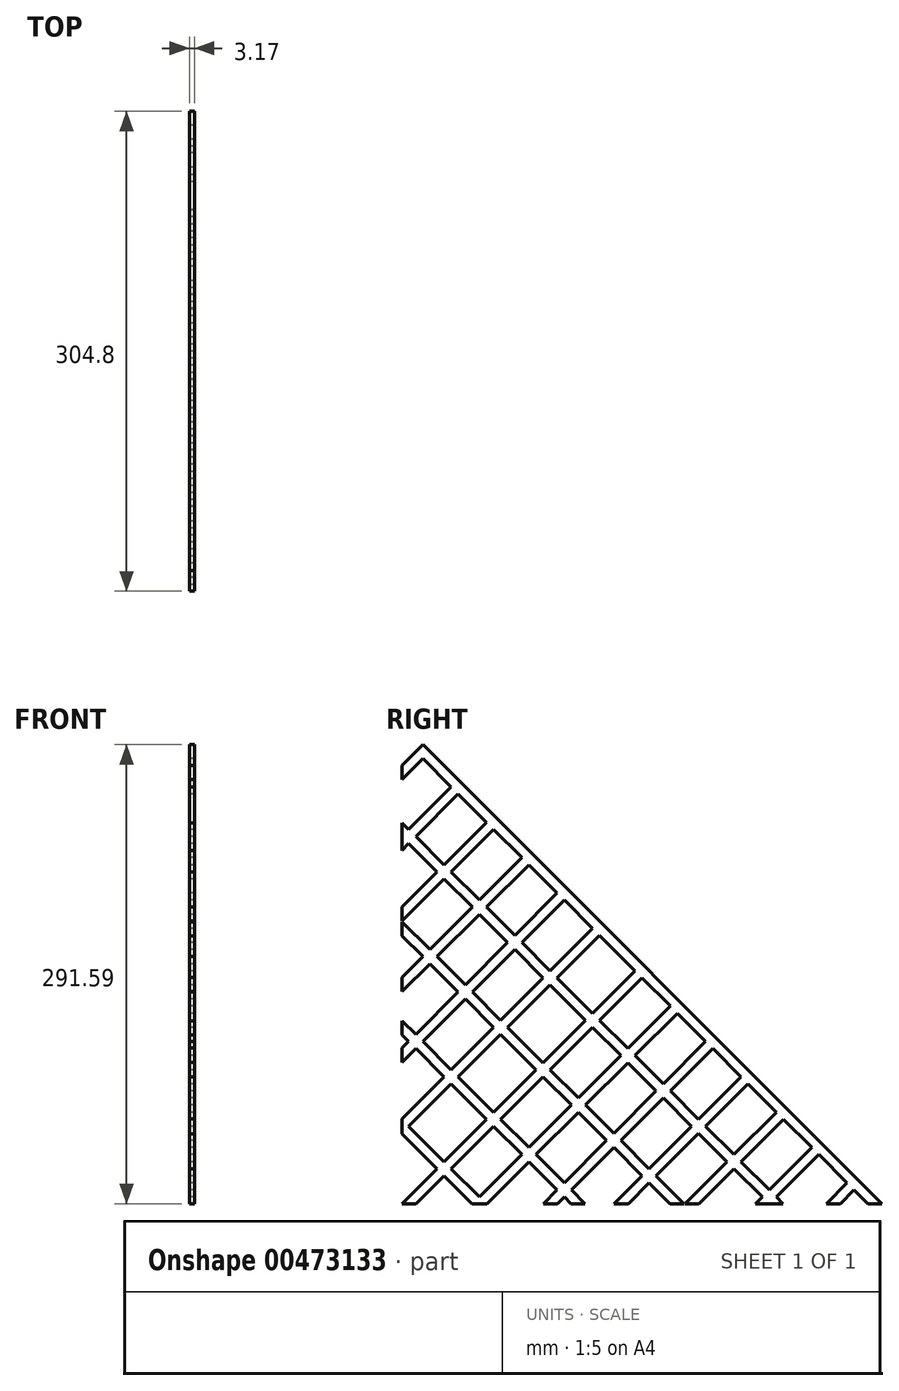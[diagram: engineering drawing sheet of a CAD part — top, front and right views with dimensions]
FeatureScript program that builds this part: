
annotation { "Feature Type Name" : "Feature", "Feature Type Description" : "" }
export const myFeature = defineFeature(function(context is Context, id is Id, definition is map)
    precondition{}
    {
        {
            var Q0;
            Q0=qCreatedBy(makeId("Right.planeOp"),FACE);
            var sketch = newSketch(context, id + "F0", { "sketchPlane" : qUnion([Q0])});
            skLineSegment(sketch, "E0.bottom", {"start": v(0, 0) * mm, "end": v(304.8, 0) * mm, "construction": true});
            skLineSegment(sketch, "E0.top", {"start": v(0, 304.8) * mm, "end": v(304.8, 304.8) * mm, "construction": true});
            skLineSegment(sketch, "E0.left", {"start": v(0, 0) * mm, "end": v(0, 304.8) * mm, "construction": true});
            skLineSegment(sketch, "E0.right", {"start": v(304.8, 0) * mm, "end": v(304.8, 304.8) * mm, "construction": true});
            skLineSegment(sketch, "E1", {"start": v(0, 0) * mm, "end": v(304.8, 304.8) * mm});
            skLineSegment(sketch, "E2.0", {"start": v(4.5, -4.5) * mm, "end": v(309.3, 300.3) * mm});
            skLineSegment(sketch, "E3.0", {"start": v(22.45, -22.45) * mm, "end": v(327.25, 282.35) * mm});
            skLineSegment(sketch, "E4.0", {"start": v(26.94, -26.94) * mm, "end": v(331.74, 277.86) * mm});
            skLineSegment(sketch, "E5.0", {"start": v(44.9, -44.9) * mm, "end": v(349.7, 259.9) * mm});
            skLineSegment(sketch, "E6.0", {"start": v(49.4, -49.4) * mm, "end": v(354.2, 255.4) * mm});
            skLineSegment(sketch, "E7.0", {"start": v(67.35, -67.35) * mm, "end": v(372.15, 237.45) * mm});
            skLineSegment(sketch, "E8.0", {"start": v(71.84, -71.84) * mm, "end": v(376.64, 232.96) * mm});
            skLineSegment(sketch, "E9.0", {"start": v(89.8, -89.8) * mm, "end": v(394.6, 215) * mm});
            skLineSegment(sketch, "E10.0", {"start": v(94.3, -94.3) * mm, "end": v(399.1, 210.5) * mm});
            skLineSegment(sketch, "E11.0", {"start": v(112.25, -112.25) * mm, "end": v(417.05, 192.55) * mm});
            skLineSegment(sketch, "E12.0", {"start": v(116.74, -116.74) * mm, "end": v(421.54, 188.06) * mm});
            skLineSegment(sketch, "E13.0", {"start": v(134.7, -134.7) * mm, "end": v(439.5, 170.1) * mm});
            skLineSegment(sketch, "E14.0", {"start": v(139.2, -139.2) * mm, "end": v(444, 165.6) * mm});
            skLineSegment(sketch, "E15.MirrorCS", {"start": v(-26.94, 26.94) * mm, "end": v(277.86, 331.74) * mm});
            skLineSegment(sketch, "E16.MirrorCS", {"start": v(-22.45, 22.45) * mm, "end": v(282.35, 327.25) * mm});
            skLineSegment(sketch, "E17.MirrorCS", {"start": v(-116.74, 116.74) * mm, "end": v(-27.2, 206.28) * mm});
            skLineSegment(sketch, "E18.MirrorCS", {"start": v(-112.25, 112.25) * mm, "end": v(-22.71, 201.8) * mm});
            skLineSegment(sketch, "E19.MirrorCS", {"start": v(-134.7, 134.7) * mm, "end": v(-13.73, 255.67) * mm});
            skLineSegment(sketch, "E20.MirrorCS", {"start": v(-139.2, 139.2) * mm, "end": v(-18.22, 260.16) * mm});
            skLineSegment(sketch, "E21.MirrorCS", {"start": v(-94.3, 94.3) * mm, "end": v(-4.75, 183.83) * mm});
            skLineSegment(sketch, "E22.MirrorCS", {"start": v(-49.4, 49.4) * mm, "end": v(255.4, 354.2) * mm});
            skLineSegment(sketch, "E23.MirrorCS", {"start": v(-71.84, 71.84) * mm, "end": v(232.96, 376.64) * mm});
            skLineSegment(sketch, "E24.MirrorCS", {"start": v(-67.35, 67.35) * mm, "end": v(237.45, 372.15) * mm});
            skLineSegment(sketch, "E25.MirrorCS", {"start": v(-44.9, 44.9) * mm, "end": v(259.9, 349.7) * mm});
            skLineSegment(sketch, "E26.MirrorCS", {"start": v(-89.8, 89.8) * mm, "end": v(-4.75, 174.85) * mm});
            skLineSegment(sketch, "E27", {"start": v(0, 304.8) * mm, "end": v(304.8, 0) * mm});
            skLineSegment(sketch, "E28.0", {"start": v(-4.5, 300.3) * mm, "end": v(300.3, -4.5) * mm});
            skLineSegment(sketch, "E29.0", {"start": v(-31.43, 273.37) * mm, "end": v(-13.73, 255.67) * mm});
            skLineSegment(sketch, "E30.0", {"start": v(-35.92, 268.88) * mm, "end": v(-18.22, 251.18) * mm});
            skLineSegment(sketch, "E31.0", {"start": v(-62.86, 241.94) * mm, "end": v(-4.75, 183.83) * mm});
            skLineSegment(sketch, "E32.0", {"start": v(-67.35, 237.45) * mm, "end": v(237.45, -67.35) * mm});
            skLineSegment(sketch, "E33.0", {"start": v(-94.3, 210.5) * mm, "end": v(210.5, -94.3) * mm});
            skLineSegment(sketch, "E34.0", {"start": v(-98.78, 206.02) * mm, "end": v(206.02, -98.78) * mm});
            skLineSegment(sketch, "E35.0", {"start": v(-125.72, 179.08) * mm, "end": v(179.08, -125.72) * mm});
            skLineSegment(sketch, "E36.0", {"start": v(-130.21, 174.59) * mm, "end": v(174.59, -130.21) * mm});
            skLineSegment(sketch, "E37.MirrorCS", {"start": v(31.43, 336.23) * mm, "end": v(336.23, 31.43) * mm});
            skLineSegment(sketch, "E38.MirrorCS", {"start": v(35.92, 340.72) * mm, "end": v(340.72, 35.92) * mm});
            skLineSegment(sketch, "E39.MirrorCS", {"start": v(62.86, 367.66) * mm, "end": v(367.66, 62.86) * mm});
            skLineSegment(sketch, "E40.MirrorCS", {"start": v(67.35, 372.15) * mm, "end": v(372.15, 67.35) * mm});
            skLineSegment(sketch, "E41.MirrorCS", {"start": v(94.3, 399.1) * mm, "end": v(399.1, 94.3) * mm});
            skLineSegment(sketch, "E42.MirrorCS", {"start": v(98.78, 403.58) * mm, "end": v(403.58, 98.78) * mm});
            skLineSegment(sketch, "E43.MirrorCS", {"start": v(125.72, 430.52) * mm, "end": v(430.52, 125.72) * mm});
            skLineSegment(sketch, "E44.MirrorCS", {"start": v(130.21, 435.01) * mm, "end": v(435.01, 130.21) * mm});
            skLineSegment(sketch, "E45", {"start": v(-4.5, 300.3) * mm, "end": v(0, 304.8) * mm});
            skLineSegment(sketch, "E46", {"start": v(300.3, -4.5) * mm, "end": v(304.8, 0) * mm});
            skLineSegment(sketch, "E47", {"start": v(0, 304.8) * mm, "end": v(0, 179.08) * mm});
            skLineSegment(sketch, "E48", {"start": v(-138.6, 0) * mm, "end": v(424.03, 0) * mm});
            skLineSegment(sketch, "E49.trimOffspring", {"start": v(0, 278.39) * mm, "end": v(165.6, 444) * mm});
            skLineSegment(sketch, "E50.trimOffspring", {"start": v(0, 269.4) * mm, "end": v(170.1, 439.5) * mm});
            skLineSegment(sketch, "E51.trimOffspring", {"start": v(0, 241.94) * mm, "end": v(273.37, -31.43) * mm});
            skLineSegment(sketch, "E52.trimOffspring", {"start": v(-0.26, 233.22) * mm, "end": v(268.88, -35.92) * mm});
            skLineSegment(sketch, "E53.trimOffspring", {"start": v(-0.26, 233.22) * mm, "end": v(188.06, 421.54) * mm});
            skLineSegment(sketch, "E54.trimOffspring", {"start": v(0, 224.5) * mm, "end": v(192.55, 417.05) * mm});
            skLineSegment(sketch, "E55.trimOffspring", {"start": v(0, 188.59) * mm, "end": v(210.5, 399.1) * mm});
            skLineSegment(sketch, "E56.trimOffspring", {"start": v(0, 170.1) * mm, "end": v(0, -155.82) * mm});
            skLineSegment(sketch, "E57.trimOffspring", {"start": v(-0.26, 179.34) * mm, "end": v(215, 394.6) * mm});
            skLineSegment(sketch, "E58.trimOffspring", {"start": v(-0.26, 179.34) * mm, "end": v(241.94, -62.86) * mm});
            skLineSegment(sketch, "E59", {"start": v(0, 179.08) * mm, "end": v(0, 170.1) * mm});
            skSolve(sketch);
        }
        {
            var Q0;
            {var subQ0=sQuery(id+"F0.wireOp",EDGE,"E49.trimOffspring");var subQ1=sQuery(id+"F0.wireOp",EDGE,"E28.0");var subQ2=makeQuery(id+"F0.imprint","INTERSECT",VERTEX,{"derivedFrom":[subQ1,subQ0]});Q0=makeQuery(id+"F0.imprint","IMPRINT",FACE,{"disambiguationData":[TD([[makeQuery(id+"F0.imprint","IMPRINT",EDGE,{"disambiguationData":[TD([[subQ2,-1.0]])],"derivedFrom":subQ1}),-1.0]])]});}
            var Q1;
            {var subQ0=sQuery(id+"F0.wireOp",EDGE,"E50.trimOffspring");var subQ1=sQuery(id+"F0.wireOp",EDGE,"E27");var subQ2=makeQuery(id+"F0.imprint","INTERSECT",VERTEX,{"derivedFrom":[subQ1,subQ0]});Q1=makeQuery(id+"F0.imprint","IMPRINT",FACE,{"disambiguationData":[TD([[makeQuery(id+"F0.imprint","IMPRINT",EDGE,{"disambiguationData":[TD([[subQ2,-1.0]])],"derivedFrom":subQ1}),-1.0]])]});}
            var Q2;
            {var subQ0=sQuery(id+"F0.wireOp",EDGE,"E49.trimOffspring");var subQ1=sQuery(id+"F0.wireOp",EDGE,"E27");var subQ2=makeQuery(id+"F0.imprint","INTERSECT",VERTEX,{"derivedFrom":[subQ1,subQ0]});Q2=makeQuery(id+"F0.imprint","IMPRINT",FACE,{"disambiguationData":[TD([[makeQuery(id+"F0.imprint","IMPRINT",EDGE,{"disambiguationData":[TD([[subQ2,-1.0]])],"derivedFrom":subQ1}),-1.0]])]});}
            var Q3;
            {var subQ0=sQuery(id+"F0.wireOp",EDGE,"E53.trimOffspring");var subQ1=sQuery(id+"F0.wireOp",EDGE,"E27");var subQ2=makeQuery(id+"F0.imprint","INTERSECT",VERTEX,{"derivedFrom":[subQ1,subQ0]});Q3=makeQuery(id+"F0.imprint","IMPRINT",FACE,{"disambiguationData":[TD([[makeQuery(id+"F0.imprint","IMPRINT",EDGE,{"disambiguationData":[TD([[subQ2,-1.0]])],"derivedFrom":subQ1}),-1.0]])]});}
            var Q4;
            {var subQ0=sQuery(id+"F0.wireOp",EDGE,"E54.trimOffspring");var subQ1=sQuery(id+"F0.wireOp",EDGE,"E27");var subQ2=makeQuery(id+"F0.imprint","INTERSECT",VERTEX,{"derivedFrom":[subQ1,subQ0]});Q4=makeQuery(id+"F0.imprint","IMPRINT",FACE,{"disambiguationData":[TD([[makeQuery(id+"F0.imprint","IMPRINT",EDGE,{"disambiguationData":[TD([[subQ2,-1.0]])],"derivedFrom":subQ1}),-1.0]])]});}
            var Q5;
            {var subQ0=sQuery(id+"F0.wireOp",EDGE,"E53.trimOffspring");var subQ1=sQuery(id+"F0.wireOp",EDGE,"E28.0");var subQ2=makeQuery(id+"F0.imprint","INTERSECT",VERTEX,{"derivedFrom":[subQ1,subQ0]});Q5=makeQuery(id+"F0.imprint","IMPRINT",FACE,{"disambiguationData":[TD([[makeQuery(id+"F0.imprint","IMPRINT",EDGE,{"disambiguationData":[TD([[subQ2,-1.0]])],"derivedFrom":subQ1}),-1.0]])]});}
            var Q6;
            {var subQ0=sQuery(id+"F0.wireOp",EDGE,"E53.trimOffspring");var subQ1=sQuery(id+"F0.wireOp",EDGE,"E47");var subQ2=makeQuery(id+"F0.imprint","INTERSECT",VERTEX,{"derivedFrom":[subQ1,subQ0]});Q6=makeQuery(id+"F0.imprint","IMPRINT",FACE,{"disambiguationData":[TD([[makeQuery(id+"F0.imprint","IMPRINT",EDGE,{"disambiguationData":[TD([[subQ2,-1.0]])],"derivedFrom":subQ1}),1.0]])]});}
            var Q7;
            {var subQ0=sQuery(id+"F0.wireOp",EDGE,"E54.trimOffspring");var subQ1=sQuery(id+"F0.wireOp",EDGE,"E47");var subQ2=makeQuery(id+"F0.imprint","INTERSECT",VERTEX,{"derivedFrom":[subQ1,subQ0]});Q7=makeQuery(id+"F0.imprint","IMPRINT",FACE,{"disambiguationData":[TD([[makeQuery(id+"F0.imprint","IMPRINT",EDGE,{"disambiguationData":[TD([[subQ2,1.0]])],"derivedFrom":subQ1}),1.0]])]});}
            var Q8;
            {var subQ0=sQuery(id+"F0.wireOp",EDGE,"E51.trimOffspring");var subQ1=sQuery(id+"F0.wireOp",EDGE,"E47");var subQ2=makeQuery(id+"F0.imprint","INTERSECT",VERTEX,{"derivedFrom":[subQ1,subQ0]});Q8=makeQuery(id+"F0.imprint","IMPRINT",FACE,{"disambiguationData":[TD([[makeQuery(id+"F0.imprint","IMPRINT",EDGE,{"disambiguationData":[TD([[subQ2,-1.0]])],"derivedFrom":subQ1}),1.0]])]});}
            var Q9;
            {var subQ0=sQuery(id+"F0.wireOp",EDGE,"E54.trimOffspring");var subQ1=sQuery(id+"F0.wireOp",EDGE,"E51.trimOffspring");var subQ2=makeQuery(id+"F0.imprint","INTERSECT",VERTEX,{"derivedFrom":[subQ1,subQ0]});Q9=makeQuery(id+"F0.imprint","IMPRINT",FACE,{"disambiguationData":[TD([[makeQuery(id+"F0.imprint","IMPRINT",EDGE,{"disambiguationData":[TD([[subQ2,-1.0]])],"derivedFrom":subQ1}),-1.0]])]});}
            var Q10;
            {var subQ0=sQuery(id+"F0.wireOp",EDGE,"E55.trimOffspring");var subQ1=sQuery(id+"F0.wireOp",EDGE,"E27");var subQ2=makeQuery(id+"F0.imprint","INTERSECT",VERTEX,{"derivedFrom":[subQ1,subQ0]});Q10=makeQuery(id+"F0.imprint","IMPRINT",FACE,{"disambiguationData":[TD([[makeQuery(id+"F0.imprint","IMPRINT",EDGE,{"disambiguationData":[TD([[subQ2,-1.0]])],"derivedFrom":subQ1}),-1.0]])]});}
            var Q11;
            {var subQ0=sQuery(id+"F0.wireOp",EDGE,"E28.0");var subQ1=sQuery(id+"F0.wireOp",EDGE,"E23.MirrorCS");var subQ2=makeQuery(id+"F0.imprint","INTERSECT",VERTEX,{"derivedFrom":[subQ1,subQ0]});Q11=makeQuery(id+"F0.imprint","IMPRINT",FACE,{"disambiguationData":[TD([[makeQuery(id+"F0.imprint","IMPRINT",EDGE,{"disambiguationData":[TD([[subQ2,-1.0]])],"derivedFrom":subQ1}),1.0]])]});}
            var Q12;
            {var subQ0=sQuery(id+"F0.wireOp",EDGE,"E55.trimOffspring");var subQ1=sQuery(id+"F0.wireOp",EDGE,"E28.0");var subQ2=makeQuery(id+"F0.imprint","INTERSECT",VERTEX,{"derivedFrom":[subQ1,subQ0]});Q12=makeQuery(id+"F0.imprint","IMPRINT",FACE,{"disambiguationData":[TD([[makeQuery(id+"F0.imprint","IMPRINT",EDGE,{"disambiguationData":[TD([[subQ2,-1.0]])],"derivedFrom":subQ1}),-1.0]])]});}
            var Q13;
            {var subQ0=sQuery(id+"F0.wireOp",EDGE,"E55.trimOffspring");var subQ1=sQuery(id+"F0.wireOp",EDGE,"E51.trimOffspring");var subQ2=makeQuery(id+"F0.imprint","INTERSECT",VERTEX,{"derivedFrom":[subQ1,subQ0]});Q13=makeQuery(id+"F0.imprint","IMPRINT",FACE,{"disambiguationData":[TD([[makeQuery(id+"F0.imprint","IMPRINT",EDGE,{"disambiguationData":[TD([[subQ2,-1.0]])],"derivedFrom":subQ1}),-1.0]])]});}
            var Q14;
            {var subQ0=sQuery(id+"F0.wireOp",EDGE,"E55.trimOffspring");var subQ1=sQuery(id+"F0.wireOp",EDGE,"E47");var subQ2=makeQuery(id+"F0.imprint","INTERSECT",VERTEX,{"derivedFrom":[subQ1,subQ0]});Q14=makeQuery(id+"F0.imprint","IMPRINT",FACE,{"disambiguationData":[TD([[makeQuery(id+"F0.imprint","IMPRINT",EDGE,{"disambiguationData":[TD([[subQ2,-1.0]])],"derivedFrom":subQ1}),1.0]])]});}
            var Q15;
            {var subQ5=sQuery(id+"F0.wireOp",EDGE,"E59");Q15=makeQuery(id+"F0.imprint","IMPRINT",FACE,{"disambiguationData":[TD([[makeQuery(id+"F0.imprint","IMPRINT",EDGE,{"derivedFrom":subQ5}),1.0]])]});}
            var Q16;
            {var subQ0=sQuery(id+"F0.wireOp",EDGE,"E52.trimOffspring");var subQ1=sQuery(id+"F0.wireOp",EDGE,"E23.MirrorCS");var subQ2=makeQuery(id+"F0.imprint","INTERSECT",VERTEX,{"derivedFrom":[subQ1,subQ0]});Q16=makeQuery(id+"F0.imprint","IMPRINT",FACE,{"disambiguationData":[TD([[makeQuery(id+"F0.imprint","IMPRINT",EDGE,{"disambiguationData":[TD([[subQ2,-1.0]])],"derivedFrom":subQ1}),1.0]])]});}
            var Q17;
            {var subQ0=sQuery(id+"F0.wireOp",EDGE,"E28.0");var subQ1=sQuery(id+"F0.wireOp",EDGE,"E23.MirrorCS");var subQ2=makeQuery(id+"F0.imprint","INTERSECT",VERTEX,{"derivedFrom":[subQ1,subQ0]});Q17=makeQuery(id+"F0.imprint","IMPRINT",FACE,{"disambiguationData":[TD([[makeQuery(id+"F0.imprint","IMPRINT",EDGE,{"disambiguationData":[TD([[subQ2,-1.0]])],"derivedFrom":subQ1}),-1.0]])]});}
            var Q18;
            {var subQ0=sQuery(id+"F0.wireOp",EDGE,"E51.trimOffspring");var subQ1=sQuery(id+"F0.wireOp",EDGE,"E23.MirrorCS");var subQ2=makeQuery(id+"F0.imprint","INTERSECT",VERTEX,{"derivedFrom":[subQ1,subQ0]});Q18=makeQuery(id+"F0.imprint","IMPRINT",FACE,{"disambiguationData":[TD([[makeQuery(id+"F0.imprint","IMPRINT",EDGE,{"disambiguationData":[TD([[subQ2,-1.0]])],"derivedFrom":subQ1}),-1.0]])]});}
            var Q19;
            {var subQ0=sQuery(id+"F0.wireOp",EDGE,"E52.trimOffspring");var subQ1=sQuery(id+"F0.wireOp",EDGE,"E23.MirrorCS");var subQ2=makeQuery(id+"F0.imprint","INTERSECT",VERTEX,{"derivedFrom":[subQ1,subQ0]});Q19=makeQuery(id+"F0.imprint","IMPRINT",FACE,{"disambiguationData":[TD([[makeQuery(id+"F0.imprint","IMPRINT",EDGE,{"disambiguationData":[TD([[subQ2,-1.0]])],"derivedFrom":subQ1}),-1.0]])]});}
            var Q20;
            {var subQ0=sQuery(id+"F0.wireOp",EDGE,"E58.trimOffspring");var subQ1=sQuery(id+"F0.wireOp",EDGE,"E23.MirrorCS");var subQ2=makeQuery(id+"F0.imprint","INTERSECT",VERTEX,{"derivedFrom":[subQ1,subQ0]});Q20=makeQuery(id+"F0.imprint","IMPRINT",FACE,{"disambiguationData":[TD([[makeQuery(id+"F0.imprint","IMPRINT",EDGE,{"disambiguationData":[TD([[subQ2,-1.0]])],"derivedFrom":subQ1}),-1.0]])]});}
            var Q21;
            {var subQ0=sQuery(id+"F0.wireOp",EDGE,"E32.0");var subQ1=sQuery(id+"F0.wireOp",EDGE,"E23.MirrorCS");var subQ2=makeQuery(id+"F0.imprint","INTERSECT",VERTEX,{"derivedFrom":[subQ1,subQ0]});Q21=makeQuery(id+"F0.imprint","IMPRINT",FACE,{"disambiguationData":[TD([[makeQuery(id+"F0.imprint","IMPRINT",EDGE,{"disambiguationData":[TD([[subQ2,-1.0]])],"derivedFrom":subQ1}),-1.0]])]});}
            var Q22;
            {var subQ0=sQuery(id+"F0.wireOp",EDGE,"E56.trimOffspring");var subQ1=sQuery(id+"F0.wireOp",EDGE,"E23.MirrorCS");var subQ2=makeQuery(id+"F0.imprint","INTERSECT",VERTEX,{"derivedFrom":[subQ1,subQ0]});Q22=makeQuery(id+"F0.imprint","IMPRINT",FACE,{"disambiguationData":[TD([[makeQuery(id+"F0.imprint","IMPRINT",EDGE,{"disambiguationData":[TD([[subQ2,-1.0]])],"derivedFrom":subQ1}),-1.0]])]});}
            var Q23;
            {var subQ0=sQuery(id+"F0.wireOp",EDGE,"E28.0");var subQ1=sQuery(id+"F0.wireOp",EDGE,"E22.MirrorCS");var subQ2=makeQuery(id+"F0.imprint","INTERSECT",VERTEX,{"derivedFrom":[subQ1,subQ0]});Q23=makeQuery(id+"F0.imprint","IMPRINT",FACE,{"disambiguationData":[TD([[makeQuery(id+"F0.imprint","IMPRINT",EDGE,{"disambiguationData":[TD([[subQ2,-1.0]])],"derivedFrom":subQ1}),1.0]])]});}
            var Q24;
            {var subQ0=sQuery(id+"F0.wireOp",EDGE,"E52.trimOffspring");var subQ1=sQuery(id+"F0.wireOp",EDGE,"E22.MirrorCS");var subQ2=makeQuery(id+"F0.imprint","INTERSECT",VERTEX,{"derivedFrom":[subQ1,subQ0]});Q24=makeQuery(id+"F0.imprint","IMPRINT",FACE,{"disambiguationData":[TD([[makeQuery(id+"F0.imprint","IMPRINT",EDGE,{"disambiguationData":[TD([[subQ2,-1.0]])],"derivedFrom":subQ1}),1.0]])]});}
            var Q25;
            {var subQ0=sQuery(id+"F0.wireOp",EDGE,"E32.0");var subQ1=sQuery(id+"F0.wireOp",EDGE,"E22.MirrorCS");var subQ2=makeQuery(id+"F0.imprint","INTERSECT",VERTEX,{"derivedFrom":[subQ1,subQ0]});Q25=makeQuery(id+"F0.imprint","IMPRINT",FACE,{"disambiguationData":[TD([[makeQuery(id+"F0.imprint","IMPRINT",EDGE,{"disambiguationData":[TD([[subQ2,-1.0]])],"derivedFrom":subQ1}),1.0]])]});}
            var Q26;
            {var subQ0=sQuery(id+"F0.wireOp",EDGE,"E34.0");var subQ1=sQuery(id+"F0.wireOp",EDGE,"E22.MirrorCS");var subQ2=makeQuery(id+"F0.imprint","INTERSECT",VERTEX,{"derivedFrom":[subQ1,subQ0]});Q26=makeQuery(id+"F0.imprint","IMPRINT",FACE,{"disambiguationData":[TD([[makeQuery(id+"F0.imprint","IMPRINT",EDGE,{"disambiguationData":[TD([[subQ2,-1.0]])],"derivedFrom":subQ1}),1.0]])]});}
            var Q27;
            {var subQ0=sQuery(id+"F0.wireOp",EDGE,"E56.trimOffspring");var subQ1=sQuery(id+"F0.wireOp",EDGE,"E22.MirrorCS");var subQ2=makeQuery(id+"F0.imprint","INTERSECT",VERTEX,{"derivedFrom":[subQ1,subQ0]});Q27=makeQuery(id+"F0.imprint","IMPRINT",FACE,{"disambiguationData":[TD([[makeQuery(id+"F0.imprint","IMPRINT",EDGE,{"disambiguationData":[TD([[subQ2,-1.0]])],"derivedFrom":subQ1}),-1.0]])]});}
            var Q28;
            {var subQ0=sQuery(id+"F0.wireOp",EDGE,"E34.0");var subQ1=sQuery(id+"F0.wireOp",EDGE,"E22.MirrorCS");var subQ2=makeQuery(id+"F0.imprint","INTERSECT",VERTEX,{"derivedFrom":[subQ1,subQ0]});Q28=makeQuery(id+"F0.imprint","IMPRINT",FACE,{"disambiguationData":[TD([[makeQuery(id+"F0.imprint","IMPRINT",EDGE,{"disambiguationData":[TD([[subQ2,-1.0]])],"derivedFrom":subQ1}),-1.0]])]});}
            var Q29;
            {var subQ0=sQuery(id+"F0.wireOp",EDGE,"E33.0");var subQ1=sQuery(id+"F0.wireOp",EDGE,"E22.MirrorCS");var subQ2=makeQuery(id+"F0.imprint","INTERSECT",VERTEX,{"derivedFrom":[subQ1,subQ0]});Q29=makeQuery(id+"F0.imprint","IMPRINT",FACE,{"disambiguationData":[TD([[makeQuery(id+"F0.imprint","IMPRINT",EDGE,{"disambiguationData":[TD([[subQ2,-1.0]])],"derivedFrom":subQ1}),-1.0]])]});}
            var Q30;
            {var subQ0=sQuery(id+"F0.wireOp",EDGE,"E32.0");var subQ1=sQuery(id+"F0.wireOp",EDGE,"E22.MirrorCS");var subQ2=makeQuery(id+"F0.imprint","INTERSECT",VERTEX,{"derivedFrom":[subQ1,subQ0]});Q30=makeQuery(id+"F0.imprint","IMPRINT",FACE,{"disambiguationData":[TD([[makeQuery(id+"F0.imprint","IMPRINT",EDGE,{"disambiguationData":[TD([[subQ2,-1.0]])],"derivedFrom":subQ1}),-1.0]])]});}
            var Q31;
            {var subQ0=sQuery(id+"F0.wireOp",EDGE,"E58.trimOffspring");var subQ1=sQuery(id+"F0.wireOp",EDGE,"E22.MirrorCS");var subQ2=makeQuery(id+"F0.imprint","INTERSECT",VERTEX,{"derivedFrom":[subQ1,subQ0]});Q31=makeQuery(id+"F0.imprint","IMPRINT",FACE,{"disambiguationData":[TD([[makeQuery(id+"F0.imprint","IMPRINT",EDGE,{"disambiguationData":[TD([[subQ2,-1.0]])],"derivedFrom":subQ1}),-1.0]])]});}
            var Q32;
            {var subQ0=sQuery(id+"F0.wireOp",EDGE,"E52.trimOffspring");var subQ1=sQuery(id+"F0.wireOp",EDGE,"E22.MirrorCS");var subQ2=makeQuery(id+"F0.imprint","INTERSECT",VERTEX,{"derivedFrom":[subQ1,subQ0]});Q32=makeQuery(id+"F0.imprint","IMPRINT",FACE,{"disambiguationData":[TD([[makeQuery(id+"F0.imprint","IMPRINT",EDGE,{"disambiguationData":[TD([[subQ2,-1.0]])],"derivedFrom":subQ1}),-1.0]])]});}
            var Q33;
            {var subQ0=sQuery(id+"F0.wireOp",EDGE,"E51.trimOffspring");var subQ1=sQuery(id+"F0.wireOp",EDGE,"E22.MirrorCS");var subQ2=makeQuery(id+"F0.imprint","INTERSECT",VERTEX,{"derivedFrom":[subQ1,subQ0]});Q33=makeQuery(id+"F0.imprint","IMPRINT",FACE,{"disambiguationData":[TD([[makeQuery(id+"F0.imprint","IMPRINT",EDGE,{"disambiguationData":[TD([[subQ2,-1.0]])],"derivedFrom":subQ1}),-1.0]])]});}
            var Q34;
            {var subQ0=sQuery(id+"F0.wireOp",EDGE,"E28.0");var subQ1=sQuery(id+"F0.wireOp",EDGE,"E22.MirrorCS");var subQ2=makeQuery(id+"F0.imprint","INTERSECT",VERTEX,{"derivedFrom":[subQ1,subQ0]});Q34=makeQuery(id+"F0.imprint","IMPRINT",FACE,{"disambiguationData":[TD([[makeQuery(id+"F0.imprint","IMPRINT",EDGE,{"disambiguationData":[TD([[subQ2,-1.0]])],"derivedFrom":subQ1}),-1.0]])]});}
            var Q35;
            {var subQ0=sQuery(id+"F0.wireOp",EDGE,"E28.0");var subQ1=sQuery(id+"F0.wireOp",EDGE,"E15.MirrorCS");var subQ2=makeQuery(id+"F0.imprint","INTERSECT",VERTEX,{"derivedFrom":[subQ1,subQ0]});Q35=makeQuery(id+"F0.imprint","IMPRINT",FACE,{"disambiguationData":[TD([[makeQuery(id+"F0.imprint","IMPRINT",EDGE,{"disambiguationData":[TD([[subQ2,-1.0]])],"derivedFrom":subQ1}),1.0]])]});}
            var Q36;
            {var subQ0=sQuery(id+"F0.wireOp",EDGE,"E52.trimOffspring");var subQ1=sQuery(id+"F0.wireOp",EDGE,"E15.MirrorCS");var subQ2=makeQuery(id+"F0.imprint","INTERSECT",VERTEX,{"derivedFrom":[subQ1,subQ0]});Q36=makeQuery(id+"F0.imprint","IMPRINT",FACE,{"disambiguationData":[TD([[makeQuery(id+"F0.imprint","IMPRINT",EDGE,{"disambiguationData":[TD([[subQ2,-1.0]])],"derivedFrom":subQ1}),1.0]])]});}
            var Q37;
            {var subQ0=sQuery(id+"F0.wireOp",EDGE,"E32.0");var subQ1=sQuery(id+"F0.wireOp",EDGE,"E15.MirrorCS");var subQ2=makeQuery(id+"F0.imprint","INTERSECT",VERTEX,{"derivedFrom":[subQ1,subQ0]});Q37=makeQuery(id+"F0.imprint","IMPRINT",FACE,{"disambiguationData":[TD([[makeQuery(id+"F0.imprint","IMPRINT",EDGE,{"disambiguationData":[TD([[subQ2,-1.0]])],"derivedFrom":subQ1}),1.0]])]});}
            var Q38;
            {var subQ0=sQuery(id+"F0.wireOp",EDGE,"E34.0");var subQ1=sQuery(id+"F0.wireOp",EDGE,"E15.MirrorCS");var subQ2=makeQuery(id+"F0.imprint","INTERSECT",VERTEX,{"derivedFrom":[subQ1,subQ0]});Q38=makeQuery(id+"F0.imprint","IMPRINT",FACE,{"disambiguationData":[TD([[makeQuery(id+"F0.imprint","IMPRINT",EDGE,{"disambiguationData":[TD([[subQ2,-1.0]])],"derivedFrom":subQ1}),1.0]])]});}
            var Q39;
            {var subQ0=sQuery(id+"F0.wireOp",EDGE,"E56.trimOffspring");var subQ1=sQuery(id+"F0.wireOp",EDGE,"E16.MirrorCS");var subQ2=makeQuery(id+"F0.imprint","INTERSECT",VERTEX,{"derivedFrom":[subQ1,subQ0]});Q39=makeQuery(id+"F0.imprint","IMPRINT",FACE,{"disambiguationData":[TD([[makeQuery(id+"F0.imprint","IMPRINT",EDGE,{"disambiguationData":[TD([[subQ2,-1.0]])],"derivedFrom":subQ1}),1.0]])]});}
            var Q40;
            {var subQ0=sQuery(id+"F0.wireOp",EDGE,"E35.0");var subQ1=sQuery(id+"F0.wireOp",EDGE,"E16.MirrorCS");var subQ2=makeQuery(id+"F0.imprint","INTERSECT",VERTEX,{"derivedFrom":[subQ1,subQ0]});Q40=makeQuery(id+"F0.imprint","IMPRINT",FACE,{"disambiguationData":[TD([[makeQuery(id+"F0.imprint","IMPRINT",EDGE,{"disambiguationData":[TD([[subQ2,-1.0]])],"derivedFrom":subQ1}),1.0]])]});}
            var Q41;
            {var subQ0=sQuery(id+"F0.wireOp",EDGE,"E34.0");var subQ1=sQuery(id+"F0.wireOp",EDGE,"E16.MirrorCS");var subQ2=makeQuery(id+"F0.imprint","INTERSECT",VERTEX,{"derivedFrom":[subQ1,subQ0]});Q41=makeQuery(id+"F0.imprint","IMPRINT",FACE,{"disambiguationData":[TD([[makeQuery(id+"F0.imprint","IMPRINT",EDGE,{"disambiguationData":[TD([[subQ2,-1.0]])],"derivedFrom":subQ1}),1.0]])]});}
            var Q42;
            {var subQ0=sQuery(id+"F0.wireOp",EDGE,"E33.0");var subQ1=sQuery(id+"F0.wireOp",EDGE,"E16.MirrorCS");var subQ2=makeQuery(id+"F0.imprint","INTERSECT",VERTEX,{"derivedFrom":[subQ1,subQ0]});Q42=makeQuery(id+"F0.imprint","IMPRINT",FACE,{"disambiguationData":[TD([[makeQuery(id+"F0.imprint","IMPRINT",EDGE,{"disambiguationData":[TD([[subQ2,-1.0]])],"derivedFrom":subQ1}),1.0]])]});}
            var Q43;
            {var subQ0=sQuery(id+"F0.wireOp",EDGE,"E32.0");var subQ1=sQuery(id+"F0.wireOp",EDGE,"E16.MirrorCS");var subQ2=makeQuery(id+"F0.imprint","INTERSECT",VERTEX,{"derivedFrom":[subQ1,subQ0]});Q43=makeQuery(id+"F0.imprint","IMPRINT",FACE,{"disambiguationData":[TD([[makeQuery(id+"F0.imprint","IMPRINT",EDGE,{"disambiguationData":[TD([[subQ2,-1.0]])],"derivedFrom":subQ1}),1.0]])]});}
            var Q44;
            {var subQ0=sQuery(id+"F0.wireOp",EDGE,"E58.trimOffspring");var subQ1=sQuery(id+"F0.wireOp",EDGE,"E16.MirrorCS");var subQ2=makeQuery(id+"F0.imprint","INTERSECT",VERTEX,{"derivedFrom":[subQ1,subQ0]});Q44=makeQuery(id+"F0.imprint","IMPRINT",FACE,{"disambiguationData":[TD([[makeQuery(id+"F0.imprint","IMPRINT",EDGE,{"disambiguationData":[TD([[subQ2,-1.0]])],"derivedFrom":subQ1}),1.0]])]});}
            var Q45;
            {var subQ0=sQuery(id+"F0.wireOp",EDGE,"E52.trimOffspring");var subQ1=sQuery(id+"F0.wireOp",EDGE,"E16.MirrorCS");var subQ2=makeQuery(id+"F0.imprint","INTERSECT",VERTEX,{"derivedFrom":[subQ1,subQ0]});Q45=makeQuery(id+"F0.imprint","IMPRINT",FACE,{"disambiguationData":[TD([[makeQuery(id+"F0.imprint","IMPRINT",EDGE,{"disambiguationData":[TD([[subQ2,-1.0]])],"derivedFrom":subQ1}),1.0]])]});}
            var Q46;
            {var subQ0=sQuery(id+"F0.wireOp",EDGE,"E52.trimOffspring");var subQ1=sQuery(id+"F0.wireOp",EDGE,"E1");var subQ2=makeQuery(id+"F0.imprint","INTERSECT",VERTEX,{"derivedFrom":[subQ1,subQ0]});Q46=makeQuery(id+"F0.imprint","IMPRINT",FACE,{"disambiguationData":[TD([[makeQuery(id+"F0.imprint","IMPRINT",EDGE,{"disambiguationData":[TD([[subQ2,-1.0]])],"derivedFrom":subQ1}),1.0]])]});}
            var Q47;
            {var subQ0=sQuery(id+"F0.wireOp",EDGE,"E52.trimOffspring");var subQ1=sQuery(id+"F0.wireOp",EDGE,"E1");var subQ2=makeQuery(id+"F0.imprint","INTERSECT",VERTEX,{"derivedFrom":[subQ1,subQ0]});Q47=makeQuery(id+"F0.imprint","IMPRINT",FACE,{"disambiguationData":[TD([[makeQuery(id+"F0.imprint","IMPRINT",EDGE,{"disambiguationData":[TD([[subQ2,-1.0]])],"derivedFrom":subQ1}),-1.0]])]});}
            var Q48;
            {var subQ0=sQuery(id+"F0.wireOp",EDGE,"E58.trimOffspring");var subQ1=sQuery(id+"F0.wireOp",EDGE,"E1");var subQ2=makeQuery(id+"F0.imprint","INTERSECT",VERTEX,{"derivedFrom":[subQ1,subQ0]});Q48=makeQuery(id+"F0.imprint","IMPRINT",FACE,{"disambiguationData":[TD([[makeQuery(id+"F0.imprint","IMPRINT",EDGE,{"disambiguationData":[TD([[subQ2,-1.0]])],"derivedFrom":subQ1}),-1.0]])]});}
            var Q49;
            {var subQ0=sQuery(id+"F0.wireOp",EDGE,"E32.0");var subQ1=sQuery(id+"F0.wireOp",EDGE,"E1");var subQ2=makeQuery(id+"F0.imprint","INTERSECT",VERTEX,{"derivedFrom":[subQ1,subQ0]});Q49=makeQuery(id+"F0.imprint","IMPRINT",FACE,{"disambiguationData":[TD([[makeQuery(id+"F0.imprint","IMPRINT",EDGE,{"disambiguationData":[TD([[subQ2,-1.0]])],"derivedFrom":subQ1}),-1.0]])]});}
            var Q50;
            {var subQ0=sQuery(id+"F0.wireOp",EDGE,"E33.0");var subQ1=sQuery(id+"F0.wireOp",EDGE,"E1");var subQ2=makeQuery(id+"F0.imprint","INTERSECT",VERTEX,{"derivedFrom":[subQ1,subQ0]});Q50=makeQuery(id+"F0.imprint","IMPRINT",FACE,{"disambiguationData":[TD([[makeQuery(id+"F0.imprint","IMPRINT",EDGE,{"disambiguationData":[TD([[subQ2,-1.0]])],"derivedFrom":subQ1}),-1.0]])]});}
            var Q51;
            {var subQ0=sQuery(id+"F0.wireOp",EDGE,"E34.0");var subQ1=sQuery(id+"F0.wireOp",EDGE,"E1");var subQ2=makeQuery(id+"F0.imprint","INTERSECT",VERTEX,{"derivedFrom":[subQ1,subQ0]});Q51=makeQuery(id+"F0.imprint","IMPRINT",FACE,{"disambiguationData":[TD([[makeQuery(id+"F0.imprint","IMPRINT",EDGE,{"disambiguationData":[TD([[subQ2,-1.0]])],"derivedFrom":subQ1}),-1.0]])]});}
            var Q52;
            {var subQ0=sQuery(id+"F0.wireOp",EDGE,"E35.0");var subQ1=sQuery(id+"F0.wireOp",EDGE,"E1");var subQ2=makeQuery(id+"F0.imprint","INTERSECT",VERTEX,{"derivedFrom":[subQ1,subQ0]});Q52=makeQuery(id+"F0.imprint","IMPRINT",FACE,{"disambiguationData":[TD([[makeQuery(id+"F0.imprint","IMPRINT",EDGE,{"disambiguationData":[TD([[subQ2,-1.0]])],"derivedFrom":subQ1}),-1.0]])]});}
            var Q53;
            {var subQ0=sQuery(id+"F0.wireOp",EDGE,"E36.0");var subQ1=sQuery(id+"F0.wireOp",EDGE,"E1");var subQ2=makeQuery(id+"F0.imprint","INTERSECT",VERTEX,{"derivedFrom":[subQ1,subQ0]});Q53=makeQuery(id+"F0.imprint","IMPRINT",FACE,{"disambiguationData":[TD([[makeQuery(id+"F0.imprint","IMPRINT",EDGE,{"disambiguationData":[TD([[subQ2,-1.0]])],"derivedFrom":subQ1}),-1.0]])]});}
            var Q54;
            {var subQ0=sQuery(id+"F0.wireOp",EDGE,"E48");var subQ5=sQuery(id+"F0.wireOp",EDGE,"E2.0");var subQ6=makeQuery(id+"F0.imprint","INTERSECT",VERTEX,{"derivedFrom":[subQ5,subQ0]});Q54=makeQuery(id+"F0.imprint","IMPRINT",FACE,{"disambiguationData":[TD([[makeQuery(id+"F0.imprint","IMPRINT",EDGE,{"disambiguationData":[TD([[subQ6,-1.0]])],"derivedFrom":subQ5}),1.0]])]});}
            var Q55;
            {var subQ1=sQuery(id+"F0.wireOp",EDGE,"E36.0");var subQ3=sQuery(id+"F0.wireOp",EDGE,"E1");var subQ4=makeQuery(id+"F0.imprint","INTERSECT",VERTEX,{"derivedFrom":[subQ3,subQ1]});Q55=makeQuery(id+"F0.imprint","IMPRINT",FACE,{"disambiguationData":[TD([[makeQuery(id+"F0.imprint","IMPRINT",EDGE,{"disambiguationData":[TD([[subQ4,-1.0]])],"derivedFrom":subQ3}),1.0]])]});}
            var Q56;
            {var subQ0=sQuery(id+"F0.wireOp",EDGE,"E34.0");var subQ1=sQuery(id+"F0.wireOp",EDGE,"E1");var subQ2=makeQuery(id+"F0.imprint","INTERSECT",VERTEX,{"derivedFrom":[subQ1,subQ0]});Q56=makeQuery(id+"F0.imprint","IMPRINT",FACE,{"disambiguationData":[TD([[makeQuery(id+"F0.imprint","IMPRINT",EDGE,{"disambiguationData":[TD([[subQ2,-1.0]])],"derivedFrom":subQ1}),1.0]])]});}
            var Q57;
            {var subQ0=sQuery(id+"F0.wireOp",EDGE,"E32.0");var subQ1=sQuery(id+"F0.wireOp",EDGE,"E1");var subQ2=makeQuery(id+"F0.imprint","INTERSECT",VERTEX,{"derivedFrom":[subQ1,subQ0]});Q57=makeQuery(id+"F0.imprint","IMPRINT",FACE,{"disambiguationData":[TD([[makeQuery(id+"F0.imprint","IMPRINT",EDGE,{"disambiguationData":[TD([[subQ2,-1.0]])],"derivedFrom":subQ1}),1.0]])]});}
            var Q58;
            {var subQ0=sQuery(id+"F0.wireOp",EDGE,"E52.trimOffspring");var subQ1=sQuery(id+"F0.wireOp",EDGE,"E2.0");var subQ2=makeQuery(id+"F0.imprint","INTERSECT",VERTEX,{"derivedFrom":[subQ1,subQ0]});Q58=makeQuery(id+"F0.imprint","IMPRINT",FACE,{"disambiguationData":[TD([[makeQuery(id+"F0.imprint","IMPRINT",EDGE,{"disambiguationData":[TD([[subQ2,-1.0]])],"derivedFrom":subQ1}),-1.0]])]});}
            var Q59;
            {var subQ0=sQuery(id+"F0.wireOp",EDGE,"E52.trimOffspring");var subQ1=sQuery(id+"F0.wireOp",EDGE,"E3.0");var subQ2=makeQuery(id+"F0.imprint","INTERSECT",VERTEX,{"derivedFrom":[subQ1,subQ0]});Q59=makeQuery(id+"F0.imprint","IMPRINT",FACE,{"disambiguationData":[TD([[makeQuery(id+"F0.imprint","IMPRINT",EDGE,{"disambiguationData":[TD([[subQ2,-1.0]])],"derivedFrom":subQ1}),-1.0]])]});}
            var Q60;
            {var subQ0=sQuery(id+"F0.wireOp",EDGE,"E52.trimOffspring");var subQ1=sQuery(id+"F0.wireOp",EDGE,"E4.0");var subQ2=makeQuery(id+"F0.imprint","INTERSECT",VERTEX,{"derivedFrom":[subQ1,subQ0]});Q60=makeQuery(id+"F0.imprint","IMPRINT",FACE,{"disambiguationData":[TD([[makeQuery(id+"F0.imprint","IMPRINT",EDGE,{"disambiguationData":[TD([[subQ2,-1.0]])],"derivedFrom":subQ1}),-1.0]])]});}
            var Q61;
            {var subQ0=sQuery(id+"F0.wireOp",EDGE,"E52.trimOffspring");var subQ1=sQuery(id+"F0.wireOp",EDGE,"E5.0");var subQ2=makeQuery(id+"F0.imprint","INTERSECT",VERTEX,{"derivedFrom":[subQ1,subQ0]});Q61=makeQuery(id+"F0.imprint","IMPRINT",FACE,{"disambiguationData":[TD([[makeQuery(id+"F0.imprint","IMPRINT",EDGE,{"disambiguationData":[TD([[subQ2,-1.0]])],"derivedFrom":subQ1}),-1.0]])]});}
            var Q62;
            {var subQ0=sQuery(id+"F0.wireOp",EDGE,"E52.trimOffspring");var subQ1=sQuery(id+"F0.wireOp",EDGE,"E6.0");var subQ2=makeQuery(id+"F0.imprint","INTERSECT",VERTEX,{"derivedFrom":[subQ1,subQ0]});Q62=makeQuery(id+"F0.imprint","IMPRINT",FACE,{"disambiguationData":[TD([[makeQuery(id+"F0.imprint","IMPRINT",EDGE,{"disambiguationData":[TD([[subQ2,-1.0]])],"derivedFrom":subQ1}),-1.0]])]});}
            var Q63;
            {var subQ0=sQuery(id+"F0.wireOp",EDGE,"E52.trimOffspring");var subQ1=sQuery(id+"F0.wireOp",EDGE,"E7.0");var subQ2=makeQuery(id+"F0.imprint","INTERSECT",VERTEX,{"derivedFrom":[subQ1,subQ0]});Q63=makeQuery(id+"F0.imprint","IMPRINT",FACE,{"disambiguationData":[TD([[makeQuery(id+"F0.imprint","IMPRINT",EDGE,{"disambiguationData":[TD([[subQ2,-1.0]])],"derivedFrom":subQ1}),-1.0]])]});}
            var Q64;
            {var subQ0=sQuery(id+"F0.wireOp",EDGE,"E52.trimOffspring");var subQ1=sQuery(id+"F0.wireOp",EDGE,"E8.0");var subQ2=makeQuery(id+"F0.imprint","INTERSECT",VERTEX,{"derivedFrom":[subQ1,subQ0]});Q64=makeQuery(id+"F0.imprint","IMPRINT",FACE,{"disambiguationData":[TD([[makeQuery(id+"F0.imprint","IMPRINT",EDGE,{"disambiguationData":[TD([[subQ2,-1.0]])],"derivedFrom":subQ1}),-1.0]])]});}
            var Q65;
            {var subQ0=sQuery(id+"F0.wireOp",EDGE,"E52.trimOffspring");var subQ1=sQuery(id+"F0.wireOp",EDGE,"E10.0");var subQ2=makeQuery(id+"F0.imprint","INTERSECT",VERTEX,{"derivedFrom":[subQ1,subQ0]});Q65=makeQuery(id+"F0.imprint","IMPRINT",FACE,{"disambiguationData":[TD([[makeQuery(id+"F0.imprint","IMPRINT",EDGE,{"disambiguationData":[TD([[subQ2,-1.0]])],"derivedFrom":subQ1}),-1.0]])]});}
            var Q66;
            {var subQ0=sQuery(id+"F0.wireOp",EDGE,"E52.trimOffspring");var subQ1=sQuery(id+"F0.wireOp",EDGE,"E9.0");var subQ2=makeQuery(id+"F0.imprint","INTERSECT",VERTEX,{"derivedFrom":[subQ1,subQ0]});Q66=makeQuery(id+"F0.imprint","IMPRINT",FACE,{"disambiguationData":[TD([[makeQuery(id+"F0.imprint","IMPRINT",EDGE,{"disambiguationData":[TD([[subQ2,-1.0]])],"derivedFrom":subQ1}),-1.0]])]});}
            var Q67;
            {var subQ1=sQuery(id+"F0.wireOp",EDGE,"E11.0");var subQ7=sQuery(id+"F0.wireOp",EDGE,"E52.trimOffspring");var subQ9=makeQuery(id+"F0.imprint","INTERSECT",VERTEX,{"derivedFrom":[subQ1,subQ7]});Q67=makeQuery(id+"F0.imprint","IMPRINT",FACE,{"disambiguationData":[TD([[makeQuery(id+"F0.imprint","IMPRINT",EDGE,{"disambiguationData":[TD([[subQ9,-1.0]])],"derivedFrom":subQ1}),-1.0]])]});}
            var Q68;
            {var subQ0=sQuery(id+"F0.wireOp",EDGE,"E48");var subQ1=sQuery(id+"F0.wireOp",EDGE,"E12.0");var subQ2=makeQuery(id+"F0.imprint","INTERSECT",VERTEX,{"derivedFrom":[subQ1,subQ0]});Q68=makeQuery(id+"F0.imprint","IMPRINT",FACE,{"disambiguationData":[TD([[makeQuery(id+"F0.imprint","IMPRINT",EDGE,{"disambiguationData":[TD([[subQ2,-1.0]])],"derivedFrom":subQ1}),-1.0]])]});}
            var Q69;
            {var subQ0=sQuery(id+"F0.wireOp",EDGE,"E48");var subQ1=sQuery(id+"F0.wireOp",EDGE,"E11.0");var subQ2=makeQuery(id+"F0.imprint","INTERSECT",VERTEX,{"derivedFrom":[subQ1,subQ0]});Q69=makeQuery(id+"F0.imprint","IMPRINT",FACE,{"disambiguationData":[TD([[makeQuery(id+"F0.imprint","IMPRINT",EDGE,{"disambiguationData":[TD([[subQ2,-1.0]])],"derivedFrom":subQ1}),-1.0]])]});}
            var Q70;
            {var subQ0=sQuery(id+"F0.wireOp",EDGE,"E48");var subQ1=sQuery(id+"F0.wireOp",EDGE,"E9.0");var subQ2=makeQuery(id+"F0.imprint","INTERSECT",VERTEX,{"derivedFrom":[subQ1,subQ0]});Q70=makeQuery(id+"F0.imprint","IMPRINT",FACE,{"disambiguationData":[TD([[makeQuery(id+"F0.imprint","IMPRINT",EDGE,{"disambiguationData":[TD([[subQ2,-1.0]])],"derivedFrom":subQ1}),-1.0]])]});}
            var Q71;
            {var subQ0=sQuery(id+"F0.wireOp",EDGE,"E32.0");var subQ1=sQuery(id+"F0.wireOp",EDGE,"E8.0");var subQ2=makeQuery(id+"F0.imprint","INTERSECT",VERTEX,{"derivedFrom":[subQ1,subQ0]});Q71=makeQuery(id+"F0.imprint","IMPRINT",FACE,{"disambiguationData":[TD([[makeQuery(id+"F0.imprint","IMPRINT",EDGE,{"disambiguationData":[TD([[subQ2,-1.0]])],"derivedFrom":subQ1}),-1.0]])]});}
            var Q72;
            {var subQ0=sQuery(id+"F0.wireOp",EDGE,"E58.trimOffspring");var subQ1=sQuery(id+"F0.wireOp",EDGE,"E7.0");var subQ2=makeQuery(id+"F0.imprint","INTERSECT",VERTEX,{"derivedFrom":[subQ1,subQ0]});Q72=makeQuery(id+"F0.imprint","IMPRINT",FACE,{"disambiguationData":[TD([[makeQuery(id+"F0.imprint","IMPRINT",EDGE,{"disambiguationData":[TD([[subQ2,-1.0]])],"derivedFrom":subQ1}),-1.0]])]});}
            var Q73;
            {var subQ0=sQuery(id+"F0.wireOp",EDGE,"E32.0");var subQ1=sQuery(id+"F0.wireOp",EDGE,"E7.0");var subQ2=makeQuery(id+"F0.imprint","INTERSECT",VERTEX,{"derivedFrom":[subQ1,subQ0]});Q73=makeQuery(id+"F0.imprint","IMPRINT",FACE,{"disambiguationData":[TD([[makeQuery(id+"F0.imprint","IMPRINT",EDGE,{"disambiguationData":[TD([[subQ2,-1.0]])],"derivedFrom":subQ1}),-1.0]])]});}
            var Q74;
            {var subQ0=sQuery(id+"F0.wireOp",EDGE,"E48");var subQ1=sQuery(id+"F0.wireOp",EDGE,"E7.0");var subQ2=makeQuery(id+"F0.imprint","INTERSECT",VERTEX,{"derivedFrom":[subQ1,subQ0]});Q74=makeQuery(id+"F0.imprint","IMPRINT",FACE,{"disambiguationData":[TD([[makeQuery(id+"F0.imprint","IMPRINT",EDGE,{"disambiguationData":[TD([[subQ2,-1.0]])],"derivedFrom":subQ1}),-1.0]])]});}
            var Q75;
            {var subQ0=sQuery(id+"F0.wireOp",EDGE,"E32.0");var subQ1=sQuery(id+"F0.wireOp",EDGE,"E6.0");var subQ2=makeQuery(id+"F0.imprint","INTERSECT",VERTEX,{"derivedFrom":[subQ1,subQ0]});Q75=makeQuery(id+"F0.imprint","IMPRINT",FACE,{"disambiguationData":[TD([[makeQuery(id+"F0.imprint","IMPRINT",EDGE,{"disambiguationData":[TD([[subQ2,-1.0]])],"derivedFrom":subQ1}),-1.0]])]});}
            var Q76;
            {var subQ0=sQuery(id+"F0.wireOp",EDGE,"E32.0");var subQ1=sQuery(id+"F0.wireOp",EDGE,"E5.0");var subQ2=makeQuery(id+"F0.imprint","INTERSECT",VERTEX,{"derivedFrom":[subQ1,subQ0]});Q76=makeQuery(id+"F0.imprint","IMPRINT",FACE,{"disambiguationData":[TD([[makeQuery(id+"F0.imprint","IMPRINT",EDGE,{"disambiguationData":[TD([[subQ2,-1.0]])],"derivedFrom":subQ1}),-1.0]])]});}
            var Q77;
            {var subQ0=sQuery(id+"F0.wireOp",EDGE,"E58.trimOffspring");var subQ1=sQuery(id+"F0.wireOp",EDGE,"E5.0");var subQ2=makeQuery(id+"F0.imprint","INTERSECT",VERTEX,{"derivedFrom":[subQ1,subQ0]});Q77=makeQuery(id+"F0.imprint","IMPRINT",FACE,{"disambiguationData":[TD([[makeQuery(id+"F0.imprint","IMPRINT",EDGE,{"disambiguationData":[TD([[subQ2,-1.0]])],"derivedFrom":subQ1}),-1.0]])]});}
            var Q78;
            {var subQ0=sQuery(id+"F0.wireOp",EDGE,"E33.0");var subQ1=sQuery(id+"F0.wireOp",EDGE,"E5.0");var subQ2=makeQuery(id+"F0.imprint","INTERSECT",VERTEX,{"derivedFrom":[subQ1,subQ0]});Q78=makeQuery(id+"F0.imprint","IMPRINT",FACE,{"disambiguationData":[TD([[makeQuery(id+"F0.imprint","IMPRINT",EDGE,{"disambiguationData":[TD([[subQ2,-1.0]])],"derivedFrom":subQ1}),-1.0]])]});}
            var Q79;
            {var subQ0=sQuery(id+"F0.wireOp",EDGE,"E34.0");var subQ1=sQuery(id+"F0.wireOp",EDGE,"E5.0");var subQ2=makeQuery(id+"F0.imprint","INTERSECT",VERTEX,{"derivedFrom":[subQ1,subQ0]});Q79=makeQuery(id+"F0.imprint","IMPRINT",FACE,{"disambiguationData":[TD([[makeQuery(id+"F0.imprint","IMPRINT",EDGE,{"disambiguationData":[TD([[subQ2,-1.0]])],"derivedFrom":subQ1}),-1.0]])]});}
            var Q80;
            {var subQ0=sQuery(id+"F0.wireOp",EDGE,"E34.0");var subQ1=sQuery(id+"F0.wireOp",EDGE,"E6.0");var subQ2=makeQuery(id+"F0.imprint","INTERSECT",VERTEX,{"derivedFrom":[subQ1,subQ0]});Q80=makeQuery(id+"F0.imprint","IMPRINT",FACE,{"disambiguationData":[TD([[makeQuery(id+"F0.imprint","IMPRINT",EDGE,{"disambiguationData":[TD([[subQ2,-1.0]])],"derivedFrom":subQ1}),-1.0]])]});}
            var Q81;
            {var subQ0=sQuery(id+"F0.wireOp",EDGE,"E48");var subQ1=sQuery(id+"F0.wireOp",EDGE,"E5.0");var subQ2=makeQuery(id+"F0.imprint","INTERSECT",VERTEX,{"derivedFrom":[subQ1,subQ0]});Q81=makeQuery(id+"F0.imprint","IMPRINT",FACE,{"disambiguationData":[TD([[makeQuery(id+"F0.imprint","IMPRINT",EDGE,{"disambiguationData":[TD([[subQ2,-1.0]])],"derivedFrom":subQ1}),-1.0]])]});}
            var Q82;
            {var subQ0=sQuery(id+"F0.wireOp",EDGE,"E32.0");var subQ1=sQuery(id+"F0.wireOp",EDGE,"E2.0");var subQ2=makeQuery(id+"F0.imprint","INTERSECT",VERTEX,{"derivedFrom":[subQ1,subQ0]});Q82=makeQuery(id+"F0.imprint","IMPRINT",FACE,{"disambiguationData":[TD([[makeQuery(id+"F0.imprint","IMPRINT",EDGE,{"disambiguationData":[TD([[subQ2,-1.0]])],"derivedFrom":subQ1}),-1.0]])]});}
            var Q83;
            {var subQ0=sQuery(id+"F0.wireOp",EDGE,"E58.trimOffspring");var subQ1=sQuery(id+"F0.wireOp",EDGE,"E3.0");var subQ2=makeQuery(id+"F0.imprint","INTERSECT",VERTEX,{"derivedFrom":[subQ1,subQ0]});Q83=makeQuery(id+"F0.imprint","IMPRINT",FACE,{"disambiguationData":[TD([[makeQuery(id+"F0.imprint","IMPRINT",EDGE,{"disambiguationData":[TD([[subQ2,-1.0]])],"derivedFrom":subQ1}),-1.0]])]});}
            var Q84;
            {var subQ0=sQuery(id+"F0.wireOp",EDGE,"E32.0");var subQ1=sQuery(id+"F0.wireOp",EDGE,"E3.0");var subQ2=makeQuery(id+"F0.imprint","INTERSECT",VERTEX,{"derivedFrom":[subQ1,subQ0]});Q84=makeQuery(id+"F0.imprint","IMPRINT",FACE,{"disambiguationData":[TD([[makeQuery(id+"F0.imprint","IMPRINT",EDGE,{"disambiguationData":[TD([[subQ2,-1.0]])],"derivedFrom":subQ1}),-1.0]])]});}
            var Q85;
            {var subQ0=sQuery(id+"F0.wireOp",EDGE,"E32.0");var subQ1=sQuery(id+"F0.wireOp",EDGE,"E4.0");var subQ2=makeQuery(id+"F0.imprint","INTERSECT",VERTEX,{"derivedFrom":[subQ1,subQ0]});Q85=makeQuery(id+"F0.imprint","IMPRINT",FACE,{"disambiguationData":[TD([[makeQuery(id+"F0.imprint","IMPRINT",EDGE,{"disambiguationData":[TD([[subQ2,-1.0]])],"derivedFrom":subQ1}),-1.0]])]});}
            var Q86;
            {var subQ0=sQuery(id+"F0.wireOp",EDGE,"E33.0");var subQ1=sQuery(id+"F0.wireOp",EDGE,"E3.0");var subQ2=makeQuery(id+"F0.imprint","INTERSECT",VERTEX,{"derivedFrom":[subQ1,subQ0]});Q86=makeQuery(id+"F0.imprint","IMPRINT",FACE,{"disambiguationData":[TD([[makeQuery(id+"F0.imprint","IMPRINT",EDGE,{"disambiguationData":[TD([[subQ2,-1.0]])],"derivedFrom":subQ1}),-1.0]])]});}
            var Q87;
            {var subQ0=sQuery(id+"F0.wireOp",EDGE,"E34.0");var subQ1=sQuery(id+"F0.wireOp",EDGE,"E2.0");var subQ2=makeQuery(id+"F0.imprint","INTERSECT",VERTEX,{"derivedFrom":[subQ1,subQ0]});Q87=makeQuery(id+"F0.imprint","IMPRINT",FACE,{"disambiguationData":[TD([[makeQuery(id+"F0.imprint","IMPRINT",EDGE,{"disambiguationData":[TD([[subQ2,-1.0]])],"derivedFrom":subQ1}),-1.0]])]});}
            var Q88;
            {var subQ0=sQuery(id+"F0.wireOp",EDGE,"E34.0");var subQ1=sQuery(id+"F0.wireOp",EDGE,"E3.0");var subQ2=makeQuery(id+"F0.imprint","INTERSECT",VERTEX,{"derivedFrom":[subQ1,subQ0]});Q88=makeQuery(id+"F0.imprint","IMPRINT",FACE,{"disambiguationData":[TD([[makeQuery(id+"F0.imprint","IMPRINT",EDGE,{"disambiguationData":[TD([[subQ2,-1.0]])],"derivedFrom":subQ1}),-1.0]])]});}
            var Q89;
            {var subQ0=sQuery(id+"F0.wireOp",EDGE,"E34.0");var subQ1=sQuery(id+"F0.wireOp",EDGE,"E4.0");var subQ2=makeQuery(id+"F0.imprint","INTERSECT",VERTEX,{"derivedFrom":[subQ1,subQ0]});Q89=makeQuery(id+"F0.imprint","IMPRINT",FACE,{"disambiguationData":[TD([[makeQuery(id+"F0.imprint","IMPRINT",EDGE,{"disambiguationData":[TD([[subQ2,-1.0]])],"derivedFrom":subQ1}),-1.0]])]});}
            var Q90;
            {var subQ1=sQuery(id+"F0.wireOp",EDGE,"E3.0");var subQ5=sQuery(id+"F0.wireOp",EDGE,"E35.0");var subQ6=makeQuery(id+"F0.imprint","INTERSECT",VERTEX,{"derivedFrom":[subQ1,subQ5]});Q90=makeQuery(id+"F0.imprint","IMPRINT",FACE,{"disambiguationData":[TD([[makeQuery(id+"F0.imprint","IMPRINT",EDGE,{"disambiguationData":[TD([[subQ6,-1.0]])],"derivedFrom":subQ1}),-1.0]])]});}
            var Q91;
            {var subQ0=sQuery(id+"F0.wireOp",EDGE,"E48");var subQ1=sQuery(id+"F0.wireOp",EDGE,"E3.0");var subQ2=makeQuery(id+"F0.imprint","INTERSECT",VERTEX,{"derivedFrom":[subQ1,subQ0]});Q91=makeQuery(id+"F0.imprint","IMPRINT",FACE,{"disambiguationData":[TD([[makeQuery(id+"F0.imprint","IMPRINT",EDGE,{"disambiguationData":[TD([[subQ2,-1.0]])],"derivedFrom":subQ1}),-1.0]])]});}
            var Q92;
            {var subQ1=sQuery(id+"F0.wireOp",EDGE,"E2.0");var subQ6=sQuery(id+"F0.wireOp",EDGE,"E36.0");var subQ8=makeQuery(id+"F0.imprint","INTERSECT",VERTEX,{"derivedFrom":[subQ1,subQ6]});Q92=makeQuery(id+"F0.imprint","IMPRINT",FACE,{"disambiguationData":[TD([[makeQuery(id+"F0.imprint","IMPRINT",EDGE,{"disambiguationData":[TD([[subQ8,-1.0]])],"derivedFrom":subQ1}),-1.0]])]});}
            extrude(context, id + "F1", {"entities" : qUnion([Q0, Q1, Q2, Q3, Q4, Q5, Q6, Q7, Q8, Q9, Q10, Q11, Q12, Q13, Q14, Q15, Q16, Q17, Q18, Q19, Q20, Q21, Q22, Q23, Q24, Q25, Q26, Q27, Q28, Q29, Q30, Q31, Q32, Q33, Q34, Q35, Q36, Q37, Q38, Q39, Q40, Q41, Q42, Q43, Q44, Q45, Q46, Q47, Q48, Q49, Q50, Q51, Q52, Q53, Q54, Q55, Q56, Q57, Q58, Q59, Q60, Q61, Q62, Q63, Q64, Q65, Q66, Q67, Q68, Q69, Q70, Q71, Q72, Q73, Q74, Q75, Q76, Q77, Q78, Q79, Q80, Q81, Q82, Q83, Q84, Q85, Q86, Q87, Q88, Q89, Q90, Q91, Q92]), "depth" : 3.17 * mm});
        }
        {
            var Q0;
            {var subQ0=sQuery(id+"F0.wireOp",EDGE,"E28.0");var subQ1=sQuery(id+"F0.wireOp",EDGE,"E16.MirrorCS");var subQ2=makeQuery(id+"F0.imprint","INTERSECT",VERTEX,{"derivedFrom":[subQ1,subQ0]});Q0=makeQuery(id+"F0.imprint","IMPRINT",FACE,{"disambiguationData":[TD([[makeQuery(id+"F0.imprint","IMPRINT",EDGE,{"disambiguationData":[TD([[subQ2,-1.0]])],"derivedFrom":subQ1}),1.0]])]});}
            var Q1;
            {var subQ0=sQuery(id+"F0.wireOp",EDGE,"E28.0");var subQ1=sQuery(id+"F0.wireOp",EDGE,"E1");var subQ2=makeQuery(id+"F0.imprint","INTERSECT",VERTEX,{"derivedFrom":[subQ1,subQ0]});Q1=makeQuery(id+"F0.imprint","IMPRINT",FACE,{"disambiguationData":[TD([[makeQuery(id+"F0.imprint","IMPRINT",EDGE,{"disambiguationData":[TD([[subQ2,-1.0]])],"derivedFrom":subQ1}),1.0]])]});}
            var Q2;
            {var subQ0=sQuery(id+"F0.wireOp",EDGE,"E51.trimOffspring");var subQ1=sQuery(id+"F0.wireOp",EDGE,"E16.MirrorCS");var subQ2=makeQuery(id+"F0.imprint","INTERSECT",VERTEX,{"derivedFrom":[subQ1,subQ0]});Q2=makeQuery(id+"F0.imprint","IMPRINT",FACE,{"disambiguationData":[TD([[makeQuery(id+"F0.imprint","IMPRINT",EDGE,{"disambiguationData":[TD([[subQ2,-1.0]])],"derivedFrom":subQ1}),1.0]])]});}
            var Q3;
            {var subQ0=sQuery(id+"F0.wireOp",EDGE,"E51.trimOffspring");var subQ1=sQuery(id+"F0.wireOp",EDGE,"E1");var subQ2=makeQuery(id+"F0.imprint","INTERSECT",VERTEX,{"derivedFrom":[subQ1,subQ0]});Q3=makeQuery(id+"F0.imprint","IMPRINT",FACE,{"disambiguationData":[TD([[makeQuery(id+"F0.imprint","IMPRINT",EDGE,{"disambiguationData":[TD([[subQ2,-1.0]])],"derivedFrom":subQ1}),-1.0]])]});}
            var Q4;
            {var subQ0=sQuery(id+"F0.wireOp",EDGE,"E28.0");var subQ1=sQuery(id+"F0.wireOp",EDGE,"E1");var subQ2=makeQuery(id+"F0.imprint","INTERSECT",VERTEX,{"derivedFrom":[subQ1,subQ0]});Q4=makeQuery(id+"F0.imprint","IMPRINT",FACE,{"disambiguationData":[TD([[makeQuery(id+"F0.imprint","IMPRINT",EDGE,{"disambiguationData":[TD([[subQ2,-1.0]])],"derivedFrom":subQ1}),-1.0]])]});}
            var Q5;
            {var subQ0=sQuery(id+"F0.wireOp",EDGE,"E28.0");var subQ1=sQuery(id+"F0.wireOp",EDGE,"E2.0");var subQ2=makeQuery(id+"F0.imprint","INTERSECT",VERTEX,{"derivedFrom":[subQ1,subQ0]});Q5=makeQuery(id+"F0.imprint","IMPRINT",FACE,{"disambiguationData":[TD([[makeQuery(id+"F0.imprint","IMPRINT",EDGE,{"disambiguationData":[TD([[subQ2,-1.0]])],"derivedFrom":subQ1}),-1.0]])]});}
            var Q6;
            {var subQ0=sQuery(id+"F0.wireOp",EDGE,"E28.0");var subQ1=sQuery(id+"F0.wireOp",EDGE,"E3.0");var subQ2=makeQuery(id+"F0.imprint","INTERSECT",VERTEX,{"derivedFrom":[subQ1,subQ0]});Q6=makeQuery(id+"F0.imprint","IMPRINT",FACE,{"disambiguationData":[TD([[makeQuery(id+"F0.imprint","IMPRINT",EDGE,{"disambiguationData":[TD([[subQ2,-1.0]])],"derivedFrom":subQ1}),-1.0]])]});}
            var Q7;
            {var subQ0=sQuery(id+"F0.wireOp",EDGE,"E51.trimOffspring");var subQ1=sQuery(id+"F0.wireOp",EDGE,"E3.0");var subQ2=makeQuery(id+"F0.imprint","INTERSECT",VERTEX,{"derivedFrom":[subQ1,subQ0]});Q7=makeQuery(id+"F0.imprint","IMPRINT",FACE,{"disambiguationData":[TD([[makeQuery(id+"F0.imprint","IMPRINT",EDGE,{"disambiguationData":[TD([[subQ2,-1.0]])],"derivedFrom":subQ1}),-1.0]])]});}
            var Q8;
            {var subQ0=sQuery(id+"F0.wireOp",EDGE,"E28.0");var subQ1=sQuery(id+"F0.wireOp",EDGE,"E4.0");var subQ2=makeQuery(id+"F0.imprint","INTERSECT",VERTEX,{"derivedFrom":[subQ1,subQ0]});Q8=makeQuery(id+"F0.imprint","IMPRINT",FACE,{"disambiguationData":[TD([[makeQuery(id+"F0.imprint","IMPRINT",EDGE,{"disambiguationData":[TD([[subQ2,-1.0]])],"derivedFrom":subQ1}),-1.0]])]});}
            var Q9;
            {var subQ0=sQuery(id+"F0.wireOp",EDGE,"E28.0");var subQ1=sQuery(id+"F0.wireOp",EDGE,"E5.0");var subQ2=makeQuery(id+"F0.imprint","INTERSECT",VERTEX,{"derivedFrom":[subQ1,subQ0]});Q9=makeQuery(id+"F0.imprint","IMPRINT",FACE,{"disambiguationData":[TD([[makeQuery(id+"F0.imprint","IMPRINT",EDGE,{"disambiguationData":[TD([[subQ2,-1.0]])],"derivedFrom":subQ1}),-1.0]])]});}
            var Q10;
            {var subQ0=sQuery(id+"F0.wireOp",EDGE,"E51.trimOffspring");var subQ1=sQuery(id+"F0.wireOp",EDGE,"E5.0");var subQ2=makeQuery(id+"F0.imprint","INTERSECT",VERTEX,{"derivedFrom":[subQ1,subQ0]});Q10=makeQuery(id+"F0.imprint","IMPRINT",FACE,{"disambiguationData":[TD([[makeQuery(id+"F0.imprint","IMPRINT",EDGE,{"disambiguationData":[TD([[subQ2,-1.0]])],"derivedFrom":subQ1}),-1.0]])]});}
            var Q11;
            {var subQ0=sQuery(id+"F0.wireOp",EDGE,"E28.0");var subQ1=sQuery(id+"F0.wireOp",EDGE,"E6.0");var subQ2=makeQuery(id+"F0.imprint","INTERSECT",VERTEX,{"derivedFrom":[subQ1,subQ0]});Q11=makeQuery(id+"F0.imprint","IMPRINT",FACE,{"disambiguationData":[TD([[makeQuery(id+"F0.imprint","IMPRINT",EDGE,{"disambiguationData":[TD([[subQ2,-1.0]])],"derivedFrom":subQ1}),-1.0]])]});}
            var Q12;
            {var subQ0=sQuery(id+"F0.wireOp",EDGE,"E28.0");var subQ1=sQuery(id+"F0.wireOp",EDGE,"E7.0");var subQ2=makeQuery(id+"F0.imprint","INTERSECT",VERTEX,{"derivedFrom":[subQ1,subQ0]});Q12=makeQuery(id+"F0.imprint","IMPRINT",FACE,{"disambiguationData":[TD([[makeQuery(id+"F0.imprint","IMPRINT",EDGE,{"disambiguationData":[TD([[subQ2,-1.0]])],"derivedFrom":subQ1}),-1.0]])]});}
            var Q13;
            {var subQ0=sQuery(id+"F0.wireOp",EDGE,"E51.trimOffspring");var subQ1=sQuery(id+"F0.wireOp",EDGE,"E7.0");var subQ2=makeQuery(id+"F0.imprint","INTERSECT",VERTEX,{"derivedFrom":[subQ1,subQ0]});Q13=makeQuery(id+"F0.imprint","IMPRINT",FACE,{"disambiguationData":[TD([[makeQuery(id+"F0.imprint","IMPRINT",EDGE,{"disambiguationData":[TD([[subQ2,-1.0]])],"derivedFrom":subQ1}),-1.0]])]});}
            var Q14;
            {var subQ0=sQuery(id+"F0.wireOp",EDGE,"E28.0");var subQ1=sQuery(id+"F0.wireOp",EDGE,"E8.0");var subQ2=makeQuery(id+"F0.imprint","INTERSECT",VERTEX,{"derivedFrom":[subQ1,subQ0]});Q14=makeQuery(id+"F0.imprint","IMPRINT",FACE,{"disambiguationData":[TD([[makeQuery(id+"F0.imprint","IMPRINT",EDGE,{"disambiguationData":[TD([[subQ2,-1.0]])],"derivedFrom":subQ1}),-1.0]])]});}
            var Q15;
            {var subQ0=sQuery(id+"F0.wireOp",EDGE,"E28.0");var subQ1=sQuery(id+"F0.wireOp",EDGE,"E9.0");var subQ2=makeQuery(id+"F0.imprint","INTERSECT",VERTEX,{"derivedFrom":[subQ1,subQ0]});Q15=makeQuery(id+"F0.imprint","IMPRINT",FACE,{"disambiguationData":[TD([[makeQuery(id+"F0.imprint","IMPRINT",EDGE,{"disambiguationData":[TD([[subQ2,-1.0]])],"derivedFrom":subQ1}),-1.0]])]});}
            var Q16;
            {var subQ0=sQuery(id+"F0.wireOp",EDGE,"E51.trimOffspring");var subQ1=sQuery(id+"F0.wireOp",EDGE,"E9.0");var subQ2=makeQuery(id+"F0.imprint","INTERSECT",VERTEX,{"derivedFrom":[subQ1,subQ0]});Q16=makeQuery(id+"F0.imprint","IMPRINT",FACE,{"disambiguationData":[TD([[makeQuery(id+"F0.imprint","IMPRINT",EDGE,{"disambiguationData":[TD([[subQ2,-1.0]])],"derivedFrom":subQ1}),-1.0]])]});}
            var Q17;
            {var subQ0=sQuery(id+"F0.wireOp",EDGE,"E28.0");var subQ1=sQuery(id+"F0.wireOp",EDGE,"E10.0");var subQ2=makeQuery(id+"F0.imprint","INTERSECT",VERTEX,{"derivedFrom":[subQ1,subQ0]});Q17=makeQuery(id+"F0.imprint","IMPRINT",FACE,{"disambiguationData":[TD([[makeQuery(id+"F0.imprint","IMPRINT",EDGE,{"disambiguationData":[TD([[subQ2,-1.0]])],"derivedFrom":subQ1}),-1.0]])]});}
            var Q18;
            {var subQ0=sQuery(id+"F0.wireOp",EDGE,"E28.0");var subQ1=sQuery(id+"F0.wireOp",EDGE,"E11.0");var subQ2=makeQuery(id+"F0.imprint","INTERSECT",VERTEX,{"derivedFrom":[subQ1,subQ0]});Q18=makeQuery(id+"F0.imprint","IMPRINT",FACE,{"disambiguationData":[TD([[makeQuery(id+"F0.imprint","IMPRINT",EDGE,{"disambiguationData":[TD([[subQ2,-1.0]])],"derivedFrom":subQ1}),-1.0]])]});}
            var Q19;
            {var subQ0=sQuery(id+"F0.wireOp",EDGE,"E51.trimOffspring");var subQ1=sQuery(id+"F0.wireOp",EDGE,"E11.0");var subQ2=makeQuery(id+"F0.imprint","INTERSECT",VERTEX,{"derivedFrom":[subQ1,subQ0]});Q19=makeQuery(id+"F0.imprint","IMPRINT",FACE,{"disambiguationData":[TD([[makeQuery(id+"F0.imprint","IMPRINT",EDGE,{"disambiguationData":[TD([[subQ2,-1.0]])],"derivedFrom":subQ1}),-1.0]])]});}
            var Q20;
            {var subQ0=sQuery(id+"F0.wireOp",EDGE,"E28.0");var subQ1=sQuery(id+"F0.wireOp",EDGE,"E12.0");var subQ2=makeQuery(id+"F0.imprint","INTERSECT",VERTEX,{"derivedFrom":[subQ1,subQ0]});Q20=makeQuery(id+"F0.imprint","IMPRINT",FACE,{"disambiguationData":[TD([[makeQuery(id+"F0.imprint","IMPRINT",EDGE,{"disambiguationData":[TD([[subQ2,-1.0]])],"derivedFrom":subQ1}),-1.0]])]});}
            var Q21;
            {var subQ0=sQuery(id+"F0.wireOp",EDGE,"E28.0");var subQ1=sQuery(id+"F0.wireOp",EDGE,"E13.0");var subQ2=makeQuery(id+"F0.imprint","INTERSECT",VERTEX,{"derivedFrom":[subQ1,subQ0]});Q21=makeQuery(id+"F0.imprint","IMPRINT",FACE,{"disambiguationData":[TD([[makeQuery(id+"F0.imprint","IMPRINT",EDGE,{"disambiguationData":[TD([[subQ2,-1.0]])],"derivedFrom":subQ1}),-1.0]])]});}
            var Q22;
            {var subQ0=sQuery(id+"F0.wireOp",EDGE,"E27");var subQ1=sQuery(id+"F0.wireOp",EDGE,"E14.0");var subQ2=makeQuery(id+"F0.imprint","INTERSECT",VERTEX,{"derivedFrom":[subQ1,subQ0]});Q22=makeQuery(id+"F0.imprint","IMPRINT",FACE,{"disambiguationData":[TD([[makeQuery(id+"F0.imprint","IMPRINT",EDGE,{"disambiguationData":[TD([[subQ2,1.0]])],"derivedFrom":subQ1}),-1.0]])]});}
            var Q23;
            {var subQ0=sQuery(id+"F0.wireOp",EDGE,"E48");var subQ1=sQuery(id+"F0.wireOp",EDGE,"E13.0");var subQ2=makeQuery(id+"F0.imprint","INTERSECT",VERTEX,{"derivedFrom":[subQ1,subQ0]});Q23=makeQuery(id+"F0.imprint","IMPRINT",FACE,{"disambiguationData":[TD([[makeQuery(id+"F0.imprint","IMPRINT",EDGE,{"disambiguationData":[TD([[subQ2,-1.0]])],"derivedFrom":subQ1}),-1.0]])]});}
            extrude(context, id + "F2", {"entities" : qUnion([Q0, Q1, Q2, Q3, Q4, Q5, Q6, Q7, Q8, Q9, Q10, Q11, Q12, Q13, Q14, Q15, Q16, Q17, Q18, Q19, Q20, Q21, Q22, Q23]), "operationType" : NewBodyOperationType.ADD, "depth" : 3.17 * mm});
        }
    });
